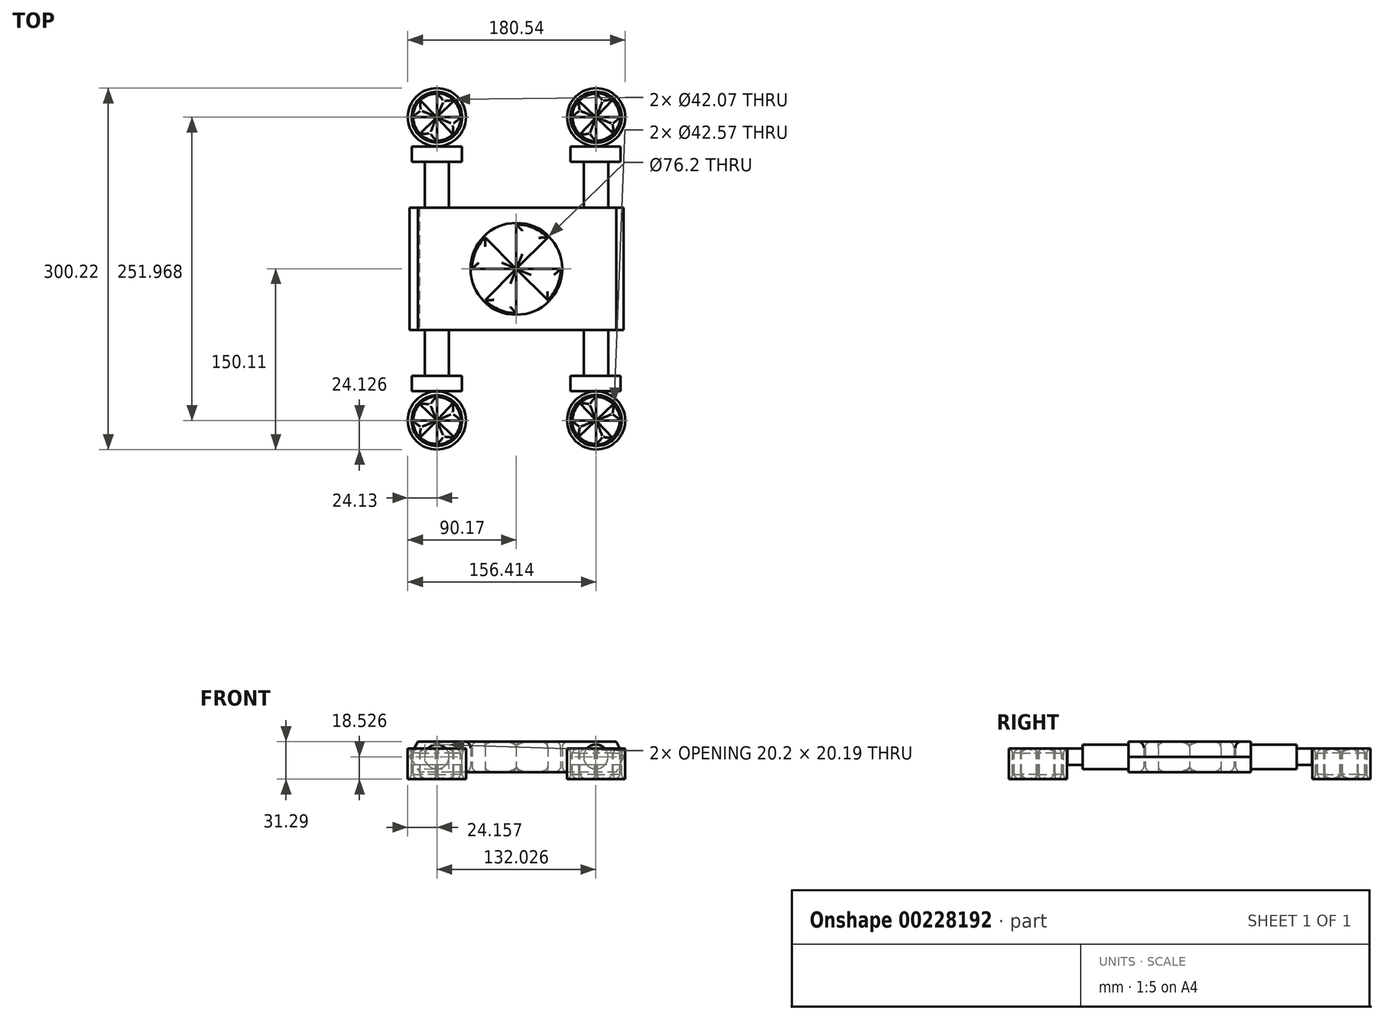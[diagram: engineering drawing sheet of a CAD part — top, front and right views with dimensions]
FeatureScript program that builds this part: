
annotation { "Feature Type Name" : "Feature", "Feature Type Description" : "" }
export const myFeature = defineFeature(function(context is Context, id is Id, definition is map)
    precondition{}
    {
        {
            var Q0;
            Q0=qCreatedBy(makeId("Top.planeOp"),FACE);
            var sketch = newSketch(context, id + "F0", { "sketchPlane" : qUnion([Q0])});
            skLineSegment(sketch, "E0.bottom", {"start": v(88.9, -50.8) * mm, "end": v(-88.9, -50.8) * mm});
            skLineSegment(sketch, "E0.top", {"start": v(88.9, 50.8) * mm, "end": v(-88.9, 50.8) * mm});
            skLineSegment(sketch, "E0.left", {"start": v(88.9, -50.8) * mm, "end": v(88.9, 50.8) * mm});
            skLineSegment(sketch, "E0.right", {"start": v(-88.9, -50.8) * mm, "end": v(-88.9, 50.8) * mm});
            skPoint(sketch, "E0.middle", {"position": v(0, 0) * mm});
            skCircle(sketch, "E1", {"center": v(0, 0) * mm, "radius": 38.1 * mm});
            skCircle(sketch, "E2", {"center": v(0, 0) * mm, "radius": 36.83 * mm});
            skCircle(sketch, "E3", {"center": v(0, 0) * mm, "radius": 1.88 * mm});
            skLineSegment(sketch, "E4", {"start": v(0, 36.83) * mm, "end": v(0, -36.83) * mm});
            skLineSegment(sketch, "E5", {"start": v(-36.83, 0) * mm, "end": v(36.83, 0) * mm});
            skLineSegment(sketch, "E6", {"start": v(0, 0) * mm, "end": v(26.04, 26.04) * mm});
            skLineSegment(sketch, "E7", {"start": v(0, 0) * mm, "end": v(-26.04, 26.04) * mm});
            skLineSegment(sketch, "E8", {"start": v(0, 0) * mm, "end": v(26.04, -26.04) * mm});
            skLineSegment(sketch, "E9", {"start": v(0, 0) * mm, "end": v(-26.04, -26.04) * mm});
            skSolve(sketch);
        }
        {
            var Q0;
            Q0 = qSketchRegion(id + "F0", true);
            extrude(context, id + "F1", {"entities" : qUnion([Q0]), "depth" : 25.4 * mm});
        }
        {
            var Q0;
            Q0=makeQuery(id+"F1.opExtrude","SWEPT_FACE",FACE,{"disambiguationData":[OSD([sQuery(id+"F0.wireOp",EDGE,"E0.bottom")])]});
            var sketch = newSketch(context, id + "F2", { "sketchPlane" : qUnion([Q0])});
            skLineSegment(sketch, "E10", {"start": v(-88.9, 12.7) * mm, "end": v(-66.04, 12.7) * mm, "construction": true});
            skLineSegment(sketch, "E11", {"start": v(88.9, 12.7) * mm, "end": v(66.04, 12.7) * mm, "construction": true});
            skPoint(sketch, "E11.endSnap0", {"position": v(88.9, 12.7) * mm});
            skCircle(sketch, "E12", {"center": v(-66.04, 12.7) * mm, "radius": 10.16 * mm});
            skCircle(sketch, "E13", {"center": v(66.04, 12.7) * mm, "radius": 10.16 * mm});
            skSolve(sketch);
        }
        {
            var Q0;
            Q0 = qSketchRegion(id + "F2", true);
            extrude(context, id + "F3", {"entities" : qUnion([Q0]), "depth" : 38.1 * mm});
        }
        {
            var Q0;
            Q0=makeQuery(id+"F3.opExtrude","CAP_FACE",FACE,{"disambiguationData":[OSD([sQuery(id+"F2.wireOp",EDGE,"E12")])],"isStart":false});
            var sketch = newSketch(context, id + "F4", { "sketchPlane" : qUnion([Q0])});
            skLineSegment(sketch, "E14.bottom", {"start": v(-45.26, 5.89) * mm, "end": v(-86.82, 5.89) * mm});
            skLineSegment(sketch, "E14.top", {"start": v(-45.26, 19.51) * mm, "end": v(-86.82, 19.51) * mm});
            skLineSegment(sketch, "E14.left", {"start": v(-45.26, 5.89) * mm, "end": v(-45.26, 19.51) * mm});
            skLineSegment(sketch, "E14.right", {"start": v(-86.82, 5.89) * mm, "end": v(-86.82, 19.51) * mm});
            skPoint(sketch, "E14.middle", {"position": v(-66.04, 12.7) * mm});
            skPoint(sketch, "E15.endSnap0", {"position": v(-45.26, 12.7) * mm});
            skLineSegment(sketch, "E16.bottom", {"start": v(86.59, 5.89) * mm, "end": v(45.02, 5.89) * mm});
            skLineSegment(sketch, "E16.top", {"start": v(86.59, 19.51) * mm, "end": v(45.02, 19.51) * mm});
            skLineSegment(sketch, "E16.left", {"start": v(86.59, 5.89) * mm, "end": v(86.59, 19.51) * mm});
            skLineSegment(sketch, "E16.right", {"start": v(45.02, 5.89) * mm, "end": v(45.02, 19.51) * mm});
            skPoint(sketch, "E16.middle", {"position": v(65.8, 12.7) * mm});
            skSolve(sketch);
        }
        {
            var Q0;
            Q0 = qSketchRegion(id + "F4", true);
            extrude(context, id + "F5", {"entities" : qUnion([Q0]), "operationType" : NewBodyOperationType.ADD, "depth" : 12.7 * mm});
        }
        {
            var Q0;
            Q0=makeQuery(id+"F5.opExtrude","SWEPT_FACE",FACE,{"disambiguationData":[OSD([sQuery(id+"F4.wireOp",EDGE,"E14.top")])]});
            var sketch = newSketch(context, id + "F6", { "sketchPlane" : qUnion([Q0])});
            skCircle(sketch, "E17", {"center": v(-66.04, -125.98) * mm, "radius": 24.13 * mm});
            skPoint(sketch, "E17.centerSnap0", {"position": v(-66.04, -101.6) * mm});
            skCircle(sketch, "E18", {"center": v(-66.04, -125.98) * mm, "radius": 21.03 * mm});
            skSolve(sketch);
        }
        {
            var Q0;
            Q0 = qSketchRegion(id + "F6", true);
            extrude(context, id + "F7", {"entities" : qUnion([Q0]), "oppositeDirection" : true, "depth" : 25.4 * mm});
        }
        {
            var Q0;
            Q0=makeQuery(id+"F5.opExtrude","SWEPT_FACE",FACE,{"disambiguationData":[OSD([sQuery(id+"F4.wireOp",EDGE,"E16.top")])]});
            var sketch = newSketch(context, id + "F8", { "sketchPlane" : qUnion([Q0])});
            skCircle(sketch, "E19", {"center": v(66.24, -125.98) * mm, "radius": 24.13 * mm});
            skCircle(sketch, "E20", {"center": v(66.24, -125.98) * mm, "radius": 21.29 * mm});
            skSolve(sketch);
        }
        {
            var Q0;
            Q0=makeQuery(id+"F6.imprint","IMPRINT",FACE,{"disambiguationData":[TD([[makeQuery(id+"F6.imprint","IMPRINT",EDGE,{"derivedFrom":sQuery(id+"F6.wireOp",EDGE,"E18")}),1.0]])]});
            var sketch = newSketch(context, id + "F9", { "sketchPlane" : qUnion([Q0])});
            skCircle(sketch, "E21", {"center": v(-66.04, -125.98) * mm, "radius": 19.93 * mm});
            skCircle(sketch, "E22", {"center": v(-66.04, -125.98) * mm, "radius": 1.2 * mm});
            skLineSegment(sketch, "E23", {"start": v(-66.04, -125.98) * mm, "end": v(-66.04, -106.36) * mm});
            skLineSegment(sketch, "E24", {"start": v(-66.04, -125.98) * mm, "end": v(-46.42, -125.98) * mm});
            skLineSegment(sketch, "E25", {"start": v(-66.04, -125.98) * mm, "end": v(-66.04, -145.6) * mm});
            skLineSegment(sketch, "E26", {"start": v(-66.04, -125.98) * mm, "end": v(-85.66, -125.98) * mm});
            skLineSegment(sketch, "E27", {"start": v(-66.04, -125.98) * mm, "end": v(-52.71, -111.58) * mm});
            skLineSegment(sketch, "E28", {"start": v(-66.04, -125.98) * mm, "end": v(-79.79, -139.98) * mm});
            skLineSegment(sketch, "E29", {"start": v(-66.04, -125.98) * mm, "end": v(-80.04, -112.24) * mm});
            skLineSegment(sketch, "E30", {"start": v(-66.04, -125.98) * mm, "end": v(-52.04, -139.73) * mm});
            skArc(sketch, "E31", {"start": v(-52.71, -111.58) * mm, "mid": v(-58.9, -107.77) * mm, "end": v(-66.04, -106.36) * mm});
            skArc(sketch, "E32", {"start": v(-52.04, -139.73) * mm, "mid": v(-47.94, -133.39) * mm, "end": v(-46.42, -125.98) * mm});
            skArc(sketch, "E33", {"start": v(-79.79, -139.98) * mm, "mid": v(-73.44, -144.09) * mm, "end": v(-66.04, -145.6) * mm});
            skArc(sketch, "E34", {"start": v(-80.04, -112.24) * mm, "mid": v(-84.14, -118.58) * mm, "end": v(-85.66, -125.98) * mm});
            skSolve(sketch);
        }
        {
            var Q0;
            Q0 = qSketchRegion(id + "F9", true);
            extrude(context, id + "F10", {"entities" : qUnion([Q0]), "oppositeDirection" : true, "depth" : 25.4 * mm});
        }
        {
            var Q0;
            Q0=sQuery(id+"F9.wireOp",EDGE,"E22");
            extrude(context, id + "F11", {"bodyType" : ToolBodyType.SURFACE, "surfaceEntities" : qUnion([Q0]), "oppositeDirection" : true, "depth" : 25.4 * mm});
        }
        {
            var Q0;
            Q0 = qSketchRegion(id + "F8", true);
            extrude(context, id + "F12", {"entities" : qUnion([Q0]), "oppositeDirection" : true, "depth" : 25.4 * mm});
        }
        {
            var Q0;
            Q0=makeQuery(id+"F12.opExtrude","CAP_FACE",FACE,{"disambiguationData":[OSD([sQuery(id+"F8.wireOp",EDGE,"E19"),sQuery(id+"F8.wireOp",EDGE,"E20")])],"isStart":true});
            var sketch = newSketch(context, id + "F13", { "sketchPlane" : qUnion([Q0])});
            skCircle(sketch, "E35", {"center": v(66.24, -125.98) * mm, "radius": 19.93 * mm});
            skCircle(sketch, "E36", {"center": v(66.24, -125.98) * mm, "radius": 1.2 * mm});
            skLineSegment(sketch, "E37", {"start": v(66.24, -125.98) * mm, "end": v(66.24, -106.36) * mm});
            skLineSegment(sketch, "E38", {"start": v(66.24, -125.98) * mm, "end": v(85.86, -125.98) * mm});
            skLineSegment(sketch, "E39", {"start": v(66.24, -125.98) * mm, "end": v(66.24, -145.6) * mm});
            skLineSegment(sketch, "E40", {"start": v(66.24, -125.98) * mm, "end": v(46.62, -125.98) * mm});
            skLineSegment(sketch, "E41", {"start": v(66.24, -125.98) * mm, "end": v(52.78, -111.7) * mm});
            skLineSegment(sketch, "E42", {"start": v(66.24, -125.98) * mm, "end": v(51.97, -139.44) * mm});
            skLineSegment(sketch, "E43", {"start": v(66.24, -125.98) * mm, "end": v(80.52, -112.52) * mm});
            skLineSegment(sketch, "E44", {"start": v(66.24, -125.98) * mm, "end": v(79.7, -140.26) * mm});
            skArc(sketch, "E45", {"start": v(80.52, -112.52) * mm, "mid": v(74, -108.03) * mm, "end": v(66.24, -106.36) * mm});
            skArc(sketch, "E46", {"start": v(52.78, -111.7) * mm, "mid": v(48.3, -118.24) * mm, "end": v(46.62, -125.98) * mm});
            skArc(sketch, "E47", {"start": v(51.97, -139.44) * mm, "mid": v(58.5, -143.94) * mm, "end": v(66.24, -145.6) * mm});
            skArc(sketch, "E48", {"start": v(79.7, -140.26) * mm, "mid": v(84.2, -133.73) * mm, "end": v(85.86, -125.98) * mm});
            skSolve(sketch);
        }
        {
            var Q0;
            Q0 = qSketchRegion(id + "F13", true);
            extrude(context, id + "F14", {"entities" : qUnion([Q0]), "oppositeDirection" : true, "depth" : 25.4 * mm});
        }
        {
            var Q0;
            Q0=sQuery(id+"F13.wireOp",EDGE,"E36");
            extrude(context, id + "F15", {"bodyType" : ToolBodyType.SURFACE, "surfaceEntities" : qUnion([Q0]), "oppositeDirection" : true, "depth" : 25.4 * mm});
        }
        {
            var Q0;
            Q0=makeQuery(id+"F5.opExtrude","SWEPT_BODY",BODY,{"disambiguationData":[OSD([sQuery(id+"F4.wireOp",EDGE,"E14.bottom"),sQuery(id+"F4.wireOp",EDGE,"E14.top"),sQuery(id+"F4.wireOp",EDGE,"E14.left"),sQuery(id+"F4.wireOp",EDGE,"E14.right")])]});
            var Q1;
            Q1=makeQuery(id+"F3.opExtrude","SWEPT_BODY",BODY,{"disambiguationData":[OSD([sQuery(id+"F2.wireOp",EDGE,"E12")])]});
            var Q2;
            Q2=makeQuery(id+"F7.opExtrude","SWEPT_BODY",BODY,{"disambiguationData":[OSD([sQuery(id+"F6.wireOp",EDGE,"E17"),sQuery(id+"F6.wireOp",EDGE,"E18")])]});
            var Q3;
            Q3=makeQuery(id+"F10.opExtrude","SWEPT_BODY",BODY,{"disambiguationData":[OSD([sQuery(id+"F9.wireOp",EDGE,"E21"),sQuery(id+"F9.wireOp",EDGE,"E22"),sQuery(id+"F9.wireOp",EDGE,"E23"),sQuery(id+"F9.wireOp",EDGE,"E24"),sQuery(id+"F9.wireOp",EDGE,"E25"),sQuery(id+"F9.wireOp",EDGE,"E26"),sQuery(id+"F9.wireOp",EDGE,"E27"),sQuery(id+"F9.wireOp",EDGE,"E28"),sQuery(id+"F9.wireOp",EDGE,"E29"),sQuery(id+"F9.wireOp",EDGE,"E30"),sQuery(id+"F9.wireOp",EDGE,"E31"),sQuery(id+"F9.wireOp",EDGE,"E32"),sQuery(id+"F9.wireOp",EDGE,"E33"),sQuery(id+"F9.wireOp",EDGE,"E34")])]});
            var Q4;
            Q4=makeQuery(id+"F3.opExtrude","SWEPT_BODY",BODY,{"disambiguationData":[OSD([sQuery(id+"F2.wireOp",EDGE,"E13")])]});
            var Q5;
            Q5=makeQuery(id+"F5.opExtrude","SWEPT_BODY",BODY,{"disambiguationData":[OSD([sQuery(id+"F4.wireOp",EDGE,"E16.bottom"),sQuery(id+"F4.wireOp",EDGE,"E16.top"),sQuery(id+"F4.wireOp",EDGE,"E16.left"),sQuery(id+"F4.wireOp",EDGE,"E16.right")])]});
            var Q6;
            Q6=makeQuery(id+"F12.opExtrude","SWEPT_BODY",BODY,{"disambiguationData":[OSD([sQuery(id+"F8.wireOp",EDGE,"E19"),sQuery(id+"F8.wireOp",EDGE,"E20")])]});
            var Q7;
            Q7=makeQuery(id+"F14.opExtrude","SWEPT_BODY",BODY,{"disambiguationData":[OSD([sQuery(id+"F13.wireOp",EDGE,"E35"),sQuery(id+"F13.wireOp",EDGE,"E36"),sQuery(id+"F13.wireOp",EDGE,"E37"),sQuery(id+"F13.wireOp",EDGE,"E38"),sQuery(id+"F13.wireOp",EDGE,"E39"),sQuery(id+"F13.wireOp",EDGE,"E40"),sQuery(id+"F13.wireOp",EDGE,"E41"),sQuery(id+"F13.wireOp",EDGE,"E42"),sQuery(id+"F13.wireOp",EDGE,"E43"),sQuery(id+"F13.wireOp",EDGE,"E44"),sQuery(id+"F13.wireOp",EDGE,"E45"),sQuery(id+"F13.wireOp",EDGE,"E46"),sQuery(id+"F13.wireOp",EDGE,"E47"),sQuery(id+"F13.wireOp",EDGE,"E48")])]});
            var Q8;
            Q8=qCreatedBy(makeId("Front.planeOp"),FACE);
            mirror(context, id + "F16", {"operationType" : NewBodyOperationType.ADD, "entities" : qUnion([Q0, Q1, Q2, Q3, Q4, Q5, Q6, Q7]), "mirrorPlane" : qUnion([Q8])});
        }
        {
            var Q0;
            {var subQ0=sQuery(id+"F0.wireOp",EDGE,"E4");var subQ1=sQuery(id+"F0.wireOp",EDGE,"E2");var subQ2=makeQuery(id+"F0.imprint","INTERSECT",VERTEX,{"disambiguationData":[OD(0.0)],"derivedFrom":[subQ1,subQ0]});Q0=makeQuery(id+"F0.imprint","IMPRINT",FACE,{"disambiguationData":[TD([[makeQuery(id+"F0.imprint","IMPRINT",EDGE,{"disambiguationData":[TD([[subQ2,1.0]])],"derivedFrom":subQ1}),1.0]])]});}
            var Q1;
            {var subQ0=sQuery(id+"F0.wireOp",EDGE,"E5");var subQ1=sQuery(id+"F0.wireOp",EDGE,"E2");var subQ2=makeQuery(id+"F0.imprint","INTERSECT",VERTEX,{"disambiguationData":[OD(0.0)],"derivedFrom":[subQ1,subQ0]});Q1=makeQuery(id+"F0.imprint","IMPRINT",FACE,{"disambiguationData":[TD([[makeQuery(id+"F0.imprint","IMPRINT",EDGE,{"disambiguationData":[TD([[subQ2,1.0]])],"derivedFrom":subQ1}),1.0]])]});}
            var Q2;
            {var subQ0=sQuery(id+"F0.wireOp",EDGE,"E4");var subQ1=sQuery(id+"F0.wireOp",EDGE,"E2");var subQ2=makeQuery(id+"F0.imprint","INTERSECT",VERTEX,{"disambiguationData":[OD(1.0)],"derivedFrom":[subQ1,subQ0]});Q2=makeQuery(id+"F0.imprint","IMPRINT",FACE,{"disambiguationData":[TD([[makeQuery(id+"F0.imprint","IMPRINT",EDGE,{"disambiguationData":[TD([[subQ2,1.0]])],"derivedFrom":subQ1}),1.0]])]});}
            var Q3;
            {var subQ0=sQuery(id+"F0.wireOp",EDGE,"E5");var subQ1=sQuery(id+"F0.wireOp",EDGE,"E2");var subQ2=makeQuery(id+"F0.imprint","INTERSECT",VERTEX,{"disambiguationData":[OD(1.0)],"derivedFrom":[subQ1,subQ0]});Q3=makeQuery(id+"F0.imprint","IMPRINT",FACE,{"disambiguationData":[TD([[makeQuery(id+"F0.imprint","IMPRINT",EDGE,{"disambiguationData":[TD([[subQ2,1.0]])],"derivedFrom":subQ1}),1.0]])]});}
            var Q4;
            {var subQ0=sQuery(id+"F0.wireOp",EDGE,"E6");var subQ1=sQuery(id+"F0.wireOp",EDGE,"E3");var subQ2=makeQuery(id+"F0.imprint","INTERSECT",VERTEX,{"derivedFrom":[subQ1,subQ0]});Q4=makeQuery(id+"F0.imprint","IMPRINT",FACE,{"disambiguationData":[TD([[makeQuery(id+"F0.imprint","IMPRINT",EDGE,{"disambiguationData":[TD([[subQ2,-1.0]])],"derivedFrom":subQ1}),1.0]])]});}
            var Q5;
            {var subQ0=sQuery(id+"F0.wireOp",EDGE,"E5");var subQ1=sQuery(id+"F0.wireOp",EDGE,"E3");var subQ2=makeQuery(id+"F0.imprint","INTERSECT",VERTEX,{"disambiguationData":[OD(0.0)],"derivedFrom":[subQ1,subQ0]});Q5=makeQuery(id+"F0.imprint","IMPRINT",FACE,{"disambiguationData":[TD([[makeQuery(id+"F0.imprint","IMPRINT",EDGE,{"disambiguationData":[TD([[subQ2,1.0]])],"derivedFrom":subQ1}),1.0]])]});}
            var Q6;
            {var subQ0=sQuery(id+"F0.wireOp",EDGE,"E9");var subQ1=sQuery(id+"F0.wireOp",EDGE,"E3");var subQ2=makeQuery(id+"F0.imprint","INTERSECT",VERTEX,{"derivedFrom":[subQ1,subQ0]});Q6=makeQuery(id+"F0.imprint","IMPRINT",FACE,{"disambiguationData":[TD([[makeQuery(id+"F0.imprint","IMPRINT",EDGE,{"disambiguationData":[TD([[subQ2,-1.0]])],"derivedFrom":subQ1}),1.0]])]});}
            var Q7;
            {var subQ0=sQuery(id+"F0.wireOp",EDGE,"E7");var subQ1=sQuery(id+"F0.wireOp",EDGE,"E3");var subQ2=makeQuery(id+"F0.imprint","INTERSECT",VERTEX,{"derivedFrom":[subQ1,subQ0]});Q7=makeQuery(id+"F0.imprint","IMPRINT",FACE,{"disambiguationData":[TD([[makeQuery(id+"F0.imprint","IMPRINT",EDGE,{"disambiguationData":[TD([[subQ2,-1.0]])],"derivedFrom":subQ1}),1.0]])]});}
            extrude(context, id + "F17", {"entities" : qUnion([Q0, Q1, Q2, Q3, Q4, Q5, Q6, Q7]), "depth" : 25.4 * mm});
        }
        {
            var Q0;
            Q0=makeQuery(id+"F1.opExtrude","SWEPT_FACE",FACE,{"disambiguationData":[OSD([sQuery(id+"F0.wireOp",EDGE,"E0.bottom")])]});
            var sketch = newSketch(context, id + "F18", { "sketchPlane" : qUnion([Q0])});
            skLineSegment(sketch, "E49", {"start": v(-81.75, 25.4) * mm, "end": v(-88.9, 12.7) * mm});
            skLineSegment(sketch, "E50", {"start": v(-88.9, 12.7) * mm, "end": v(-80.36, 0) * mm});
            skLineSegment(sketch, "E51", {"start": v(-80.36, 0) * mm, "end": v(-81.75, 25.4) * mm});
            skLineSegment(sketch, "E52", {"start": v(83.02, 25.4) * mm, "end": v(88.9, 12.7) * mm});
            skLineSegment(sketch, "E53", {"start": v(88.9, 12.7) * mm, "end": v(83.05, 0) * mm});
            skLineSegment(sketch, "E54", {"start": v(83.05, 0) * mm, "end": v(83.02, 25.4) * mm});
            skSolve(sketch);
        }
        {
            var Q0;
            {var subQ0=sQuery(id+"F18.wireOp",EDGE,"E49");Q0=makeQuery(id+"F18.imprint","IMPRINT",FACE,{"disambiguationData":[TD([[makeQuery(id+"F18.imprint","IMPRINT",EDGE,{"derivedFrom":subQ0}),-1.0]])]});}
            var Q1;
            {var subQ0=sQuery(id+"F18.wireOp",EDGE,"E50");Q1=makeQuery(id+"F18.imprint","IMPRINT",FACE,{"disambiguationData":[TD([[makeQuery(id+"F18.imprint","IMPRINT",EDGE,{"derivedFrom":subQ0}),-1.0]])]});}
            var Q2;
            {var subQ0=sQuery(id+"F18.wireOp",EDGE,"E52");Q2=makeQuery(id+"F18.imprint","IMPRINT",FACE,{"disambiguationData":[TD([[makeQuery(id+"F18.imprint","IMPRINT",EDGE,{"derivedFrom":subQ0}),1.0]])]});}
            var Q3;
            {var subQ0=sQuery(id+"F18.wireOp",EDGE,"E53");Q3=makeQuery(id+"F18.imprint","IMPRINT",FACE,{"disambiguationData":[TD([[makeQuery(id+"F18.imprint","IMPRINT",EDGE,{"derivedFrom":subQ0}),1.0]])]});}
            extrude(context, id + "F19", {"entities" : qUnion([Q0, Q1, Q2, Q3]), "operationType" : NewBodyOperationType.REMOVE, "oppositeDirection" : true, "depth" : 125.98 * mm});
        }
        {
            var Q0;
            Q0=makeQuery(id+"F17.opExtrude","CAP_FACE",FACE,{"disambiguationData":[OSD([sQuery(id+"F0.wireOp",EDGE,"E2"),sQuery(id+"F0.wireOp",EDGE,"E4"),sQuery(id+"F0.wireOp",EDGE,"E9")])],"isStart":false});
            var Q1;
            Q1=makeQuery(id+"F17.opExtrude","CAP_FACE",FACE,{"disambiguationData":[OSD([sQuery(id+"F0.wireOp",EDGE,"E2"),sQuery(id+"F0.wireOp",EDGE,"E5"),sQuery(id+"F0.wireOp",EDGE,"E8")])],"isStart":false});
            var Q2;
            Q2=makeQuery(id+"F17.opExtrude","CAP_FACE",FACE,{"disambiguationData":[OSD([sQuery(id+"F0.wireOp",EDGE,"E2"),sQuery(id+"F0.wireOp",EDGE,"E4"),sQuery(id+"F0.wireOp",EDGE,"E6")])],"isStart":false});
            var Q3;
            Q3=makeQuery(id+"F17.opExtrude","CAP_FACE",FACE,{"disambiguationData":[OSD([sQuery(id+"F0.wireOp",EDGE,"E2"),sQuery(id+"F0.wireOp",EDGE,"E5"),sQuery(id+"F0.wireOp",EDGE,"E7")])],"isStart":false});
            var Q4;
            Q4=makeQuery(id+"F17.opExtrude","CAP_FACE",FACE,{"disambiguationData":[OSD([sQuery(id+"F0.wireOp",EDGE,"E2"),sQuery(id+"F0.wireOp",EDGE,"E4"),sQuery(id+"F0.wireOp",EDGE,"E9")])],"isStart":true});
            var Q5;
            Q5=makeQuery(id+"F17.opExtrude","CAP_FACE",FACE,{"disambiguationData":[OSD([sQuery(id+"F0.wireOp",EDGE,"E2"),sQuery(id+"F0.wireOp",EDGE,"E5"),sQuery(id+"F0.wireOp",EDGE,"E8")])],"isStart":true});
            var Q6;
            Q6=makeQuery(id+"F17.opExtrude","CAP_FACE",FACE,{"disambiguationData":[OSD([sQuery(id+"F0.wireOp",EDGE,"E2"),sQuery(id+"F0.wireOp",EDGE,"E4"),sQuery(id+"F0.wireOp",EDGE,"E6")])],"isStart":true});
            var Q7;
            Q7=makeQuery(id+"F17.opExtrude","CAP_FACE",FACE,{"disambiguationData":[OSD([sQuery(id+"F0.wireOp",EDGE,"E2"),sQuery(id+"F0.wireOp",EDGE,"E5"),sQuery(id+"F0.wireOp",EDGE,"E7")])],"isStart":true});
            fillet(context, id + "F20", {"entities" : qUnion([Q0, Q1, Q2, Q3, Q4, Q5, Q6, Q7]), "radius" : 5.08 * mm, "tangentPropagation" : true, "allowEdgeOverflow" : false});
        }
        {
            var Q0;
            Q0=makeQuery(id+"F16.opPattern","COPY",FACE,{"derivedFrom":makeQuery(id+"F10.opExtrude","CAP_FACE",FACE,{"disambiguationData":[OSD([sQuery(id+"F9.wireOp",EDGE,"E21"),sQuery(id+"F9.wireOp",EDGE,"E22"),sQuery(id+"F9.wireOp",EDGE,"E23"),sQuery(id+"F9.wireOp",EDGE,"E24"),sQuery(id+"F9.wireOp",EDGE,"E25"),sQuery(id+"F9.wireOp",EDGE,"E26"),sQuery(id+"F9.wireOp",EDGE,"E27"),sQuery(id+"F9.wireOp",EDGE,"E28"),sQuery(id+"F9.wireOp",EDGE,"E29"),sQuery(id+"F9.wireOp",EDGE,"E30"),sQuery(id+"F9.wireOp",EDGE,"E31"),sQuery(id+"F9.wireOp",EDGE,"E32"),sQuery(id+"F9.wireOp",EDGE,"E33"),sQuery(id+"F9.wireOp",EDGE,"E34")])],"isStart":true}),"instanceName":"1"});
            var Q1;
            Q1=makeQuery(id+"F16.opPattern","COPY",FACE,{"derivedFrom":makeQuery(id+"F14.opExtrude","CAP_FACE",FACE,{"disambiguationData":[OSD([sQuery(id+"F13.wireOp",EDGE,"E35"),sQuery(id+"F13.wireOp",EDGE,"E36"),sQuery(id+"F13.wireOp",EDGE,"E37"),sQuery(id+"F13.wireOp",EDGE,"E38"),sQuery(id+"F13.wireOp",EDGE,"E39"),sQuery(id+"F13.wireOp",EDGE,"E40"),sQuery(id+"F13.wireOp",EDGE,"E41"),sQuery(id+"F13.wireOp",EDGE,"E42"),sQuery(id+"F13.wireOp",EDGE,"E43"),sQuery(id+"F13.wireOp",EDGE,"E44"),sQuery(id+"F13.wireOp",EDGE,"E45"),sQuery(id+"F13.wireOp",EDGE,"E46"),sQuery(id+"F13.wireOp",EDGE,"E47"),sQuery(id+"F13.wireOp",EDGE,"E48")])],"isStart":true}),"instanceName":"1"});
            var Q2;
            Q2=makeQuery(id+"F14.opExtrude","CAP_FACE",FACE,{"disambiguationData":[OSD([sQuery(id+"F13.wireOp",EDGE,"E35"),sQuery(id+"F13.wireOp",EDGE,"E36"),sQuery(id+"F13.wireOp",EDGE,"E37"),sQuery(id+"F13.wireOp",EDGE,"E38"),sQuery(id+"F13.wireOp",EDGE,"E39"),sQuery(id+"F13.wireOp",EDGE,"E40"),sQuery(id+"F13.wireOp",EDGE,"E41"),sQuery(id+"F13.wireOp",EDGE,"E42"),sQuery(id+"F13.wireOp",EDGE,"E43"),sQuery(id+"F13.wireOp",EDGE,"E44"),sQuery(id+"F13.wireOp",EDGE,"E45"),sQuery(id+"F13.wireOp",EDGE,"E46"),sQuery(id+"F13.wireOp",EDGE,"E47"),sQuery(id+"F13.wireOp",EDGE,"E48")])],"isStart":true});
            var Q3;
            Q3=makeQuery(id+"F10.opExtrude","CAP_FACE",FACE,{"disambiguationData":[OSD([sQuery(id+"F9.wireOp",EDGE,"E21"),sQuery(id+"F9.wireOp",EDGE,"E22"),sQuery(id+"F9.wireOp",EDGE,"E23"),sQuery(id+"F9.wireOp",EDGE,"E24"),sQuery(id+"F9.wireOp",EDGE,"E25"),sQuery(id+"F9.wireOp",EDGE,"E26"),sQuery(id+"F9.wireOp",EDGE,"E27"),sQuery(id+"F9.wireOp",EDGE,"E28"),sQuery(id+"F9.wireOp",EDGE,"E29"),sQuery(id+"F9.wireOp",EDGE,"E30"),sQuery(id+"F9.wireOp",EDGE,"E31"),sQuery(id+"F9.wireOp",EDGE,"E32"),sQuery(id+"F9.wireOp",EDGE,"E33"),sQuery(id+"F9.wireOp",EDGE,"E34")])],"isStart":true});
            var Q4;
            Q4=makeQuery(id+"F16.opPattern","COPY",FACE,{"derivedFrom":makeQuery(id+"F10.opExtrude","CAP_FACE",FACE,{"disambiguationData":[OSD([sQuery(id+"F9.wireOp",EDGE,"E21"),sQuery(id+"F9.wireOp",EDGE,"E22"),sQuery(id+"F9.wireOp",EDGE,"E23"),sQuery(id+"F9.wireOp",EDGE,"E24"),sQuery(id+"F9.wireOp",EDGE,"E25"),sQuery(id+"F9.wireOp",EDGE,"E26"),sQuery(id+"F9.wireOp",EDGE,"E27"),sQuery(id+"F9.wireOp",EDGE,"E28"),sQuery(id+"F9.wireOp",EDGE,"E29"),sQuery(id+"F9.wireOp",EDGE,"E30"),sQuery(id+"F9.wireOp",EDGE,"E31"),sQuery(id+"F9.wireOp",EDGE,"E32"),sQuery(id+"F9.wireOp",EDGE,"E33"),sQuery(id+"F9.wireOp",EDGE,"E34")])],"isStart":false}),"instanceName":"1"});
            var Q5;
            Q5=makeQuery(id+"F16.opPattern","COPY",FACE,{"derivedFrom":makeQuery(id+"F14.opExtrude","CAP_FACE",FACE,{"disambiguationData":[OSD([sQuery(id+"F13.wireOp",EDGE,"E35"),sQuery(id+"F13.wireOp",EDGE,"E36"),sQuery(id+"F13.wireOp",EDGE,"E37"),sQuery(id+"F13.wireOp",EDGE,"E38"),sQuery(id+"F13.wireOp",EDGE,"E39"),sQuery(id+"F13.wireOp",EDGE,"E40"),sQuery(id+"F13.wireOp",EDGE,"E41"),sQuery(id+"F13.wireOp",EDGE,"E42"),sQuery(id+"F13.wireOp",EDGE,"E43"),sQuery(id+"F13.wireOp",EDGE,"E44"),sQuery(id+"F13.wireOp",EDGE,"E45"),sQuery(id+"F13.wireOp",EDGE,"E46"),sQuery(id+"F13.wireOp",EDGE,"E47"),sQuery(id+"F13.wireOp",EDGE,"E48")])],"isStart":false}),"instanceName":"1"});
            var Q6;
            Q6=makeQuery(id+"F14.opExtrude","CAP_FACE",FACE,{"disambiguationData":[OSD([sQuery(id+"F13.wireOp",EDGE,"E35"),sQuery(id+"F13.wireOp",EDGE,"E36"),sQuery(id+"F13.wireOp",EDGE,"E37"),sQuery(id+"F13.wireOp",EDGE,"E38"),sQuery(id+"F13.wireOp",EDGE,"E39"),sQuery(id+"F13.wireOp",EDGE,"E40"),sQuery(id+"F13.wireOp",EDGE,"E41"),sQuery(id+"F13.wireOp",EDGE,"E42"),sQuery(id+"F13.wireOp",EDGE,"E43"),sQuery(id+"F13.wireOp",EDGE,"E44"),sQuery(id+"F13.wireOp",EDGE,"E45"),sQuery(id+"F13.wireOp",EDGE,"E46"),sQuery(id+"F13.wireOp",EDGE,"E47"),sQuery(id+"F13.wireOp",EDGE,"E48")])],"isStart":false});
            var Q7;
            Q7=makeQuery(id+"F10.opExtrude","CAP_FACE",FACE,{"disambiguationData":[OSD([sQuery(id+"F9.wireOp",EDGE,"E21"),sQuery(id+"F9.wireOp",EDGE,"E22"),sQuery(id+"F9.wireOp",EDGE,"E23"),sQuery(id+"F9.wireOp",EDGE,"E24"),sQuery(id+"F9.wireOp",EDGE,"E25"),sQuery(id+"F9.wireOp",EDGE,"E26"),sQuery(id+"F9.wireOp",EDGE,"E27"),sQuery(id+"F9.wireOp",EDGE,"E28"),sQuery(id+"F9.wireOp",EDGE,"E29"),sQuery(id+"F9.wireOp",EDGE,"E30"),sQuery(id+"F9.wireOp",EDGE,"E31"),sQuery(id+"F9.wireOp",EDGE,"E32"),sQuery(id+"F9.wireOp",EDGE,"E33"),sQuery(id+"F9.wireOp",EDGE,"E34")])],"isStart":false});
            fillet(context, id + "F21", {"entities" : qUnion([Q0, Q1, Q2, Q3, Q4, Q5, Q6, Q7]), "radius" : 5.08 * mm, "tangentPropagation" : true, "allowEdgeOverflow" : false});
        }
        {
            var Q0;
            Q0=makeQuery(id+"F12.opExtrude","CAP_EDGE",EDGE,{"disambiguationData":[OSD([sQuery(id+"F8.wireOp",EDGE,"E20")])],"isStart":true});
            var Q1;
            Q1=makeQuery(id+"F7.opExtrude","CAP_EDGE",EDGE,{"disambiguationData":[OSD([sQuery(id+"F6.wireOp",EDGE,"E18")])],"isStart":true});
            var Q2;
            Q2=makeQuery(id+"F16.opPattern","COPY",FACE,{"derivedFrom":makeQuery(id+"F12.opExtrude","SWEPT_FACE",FACE,{"disambiguationData":[OSD([sQuery(id+"F8.wireOp",EDGE,"E20")])]}),"instanceName":"1"});
            var Q3;
            Q3=makeQuery(id+"F16.opPattern","COPY",EDGE,{"derivedFrom":makeQuery(id+"F7.opExtrude","CAP_EDGE",EDGE,{"disambiguationData":[OSD([sQuery(id+"F6.wireOp",EDGE,"E18")])],"isStart":true}),"instanceName":"1"});
            var Q4;
            Q4=makeQuery(id+"F16.opPattern","COPY",EDGE,{"derivedFrom":makeQuery(id+"F7.opExtrude","CAP_EDGE",EDGE,{"disambiguationData":[OSD([sQuery(id+"F6.wireOp",EDGE,"E18")])],"isStart":false}),"instanceName":"1"});
            var Q5;
            Q5=makeQuery(id+"F1.opExtrude","SWEPT_FACE",FACE,{"disambiguationData":[OSD([sQuery(id+"F0.wireOp",EDGE,"E1")])]});
            var Q6;
            Q6=makeQuery(id+"F7.opExtrude","CAP_EDGE",EDGE,{"disambiguationData":[OSD([sQuery(id+"F6.wireOp",EDGE,"E18")])],"isStart":false});
            var Q7;
            Q7=makeQuery(id+"F12.opExtrude","CAP_EDGE",EDGE,{"disambiguationData":[OSD([sQuery(id+"F8.wireOp",EDGE,"E20")])],"isStart":false});
            fillet(context, id + "F22", {"entities" : qUnion([Q0, Q1, Q2, Q3, Q4, Q5, Q6, Q7]), "radius" : 5.08 * mm, "tangentPropagation" : true, "allowEdgeOverflow" : false});
        }
    });
